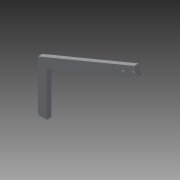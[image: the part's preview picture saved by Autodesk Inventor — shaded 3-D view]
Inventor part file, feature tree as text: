
AUTODESK INVENTOR PART (.ipt)
format: ipt  version: 2013 (Build 170138000, 138)  size: 130,048 bytes
history: native  units: in
note: dims shown in document units (in); Inventor stores cm internally (conversion verified against a paired STEP export)
features: extrude x2, sketch x2, plane x1
ambient origin geometry x8: Origin, YZ Plane, XZ Plane, XY Plane, X Axis, Y Axis, Z Axis, Center Point
bodies: Solid1 (feature_tree)
feature tree (5):
  plane  "Work Plane1"
  extrude  "Extrusion1"  Depth=19.0in
  extrude  "Extrusion2"  TaperAngle=90.0deg  [1 undecoded]
  sketch  "Sketch1"  dims[d0=2.5in d1=19.0in]
  sketch  "Sketch2"  dims[d2=3.0in d3=90.0deg d4=5.0in d5=90.0deg d6=4.0in d7=90.0deg d8=53.0in d9=90.0deg d10=21.0in d11=7.0in d12=0.5in d14=2.5in d15=0.5in d16=0.75in d17=22.5deg d18=0.5in d19=90.0deg d20=90.0deg d21=0.5in d22=112.5deg d23=23.2731in d24=90.0deg d25=10.0in d26=90.0deg d27=1.0in d28=90.0deg d29=90.0deg d30=1.0in d31=0.0in d32=22.5deg d33=1.0in d34=112.5deg d35=2.0in d36=0.0in d39=1.0in d40=2.0in d42=157.5deg d43=1.0in d44=0.0in]
note: 1 required parameter value undecoded (feature->parameter linkage not recoverable at this tier; creation-order binding heuristic only, values carry confidence <= 0.55)
